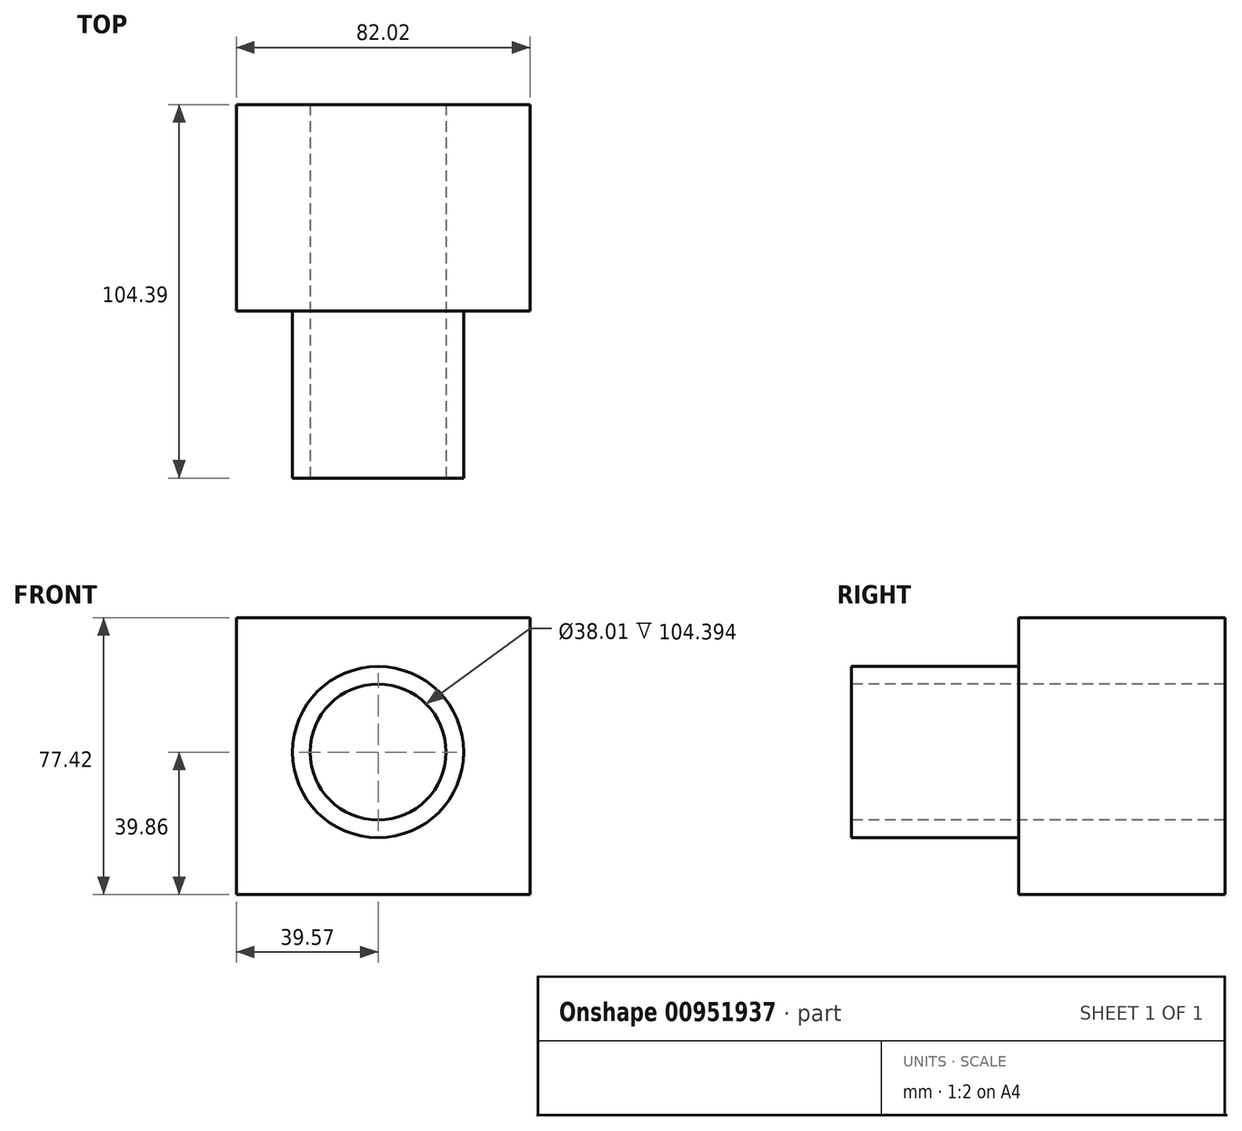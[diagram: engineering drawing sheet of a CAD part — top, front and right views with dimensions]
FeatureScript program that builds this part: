
annotation { "Feature Type Name" : "Feature", "Feature Type Description" : "" }
export const myFeature = defineFeature(function(context is Context, id is Id, definition is map)
    precondition{}
    {
        {
            var Q0;
            Q0=qCreatedBy(makeId("Front.planeOp"),FACE);
            var sketch = newSketch(context, id + "F0", { "sketchPlane" : qUnion([Q0])});
            skLineSegment(sketch, "E0.bottom", {"start": v(-39.57, 37.56) * mm, "end": v(42.45, 37.56) * mm});
            skLineSegment(sketch, "E0.top", {"start": v(-39.57, -39.86) * mm, "end": v(42.45, -39.86) * mm});
            skLineSegment(sketch, "E0.left", {"start": v(-39.57, 37.56) * mm, "end": v(-39.57, -39.86) * mm});
            skLineSegment(sketch, "E0.right", {"start": v(42.45, 37.56) * mm, "end": v(42.45, -39.86) * mm});
            skSolve(sketch);
        }
        {
            var Q0;
            Q0=makeQuery(id+"F0.imprint","IMPRINT",FACE,{"disambiguationData":[TD([[makeQuery(id+"F0.imprint","IMPRINT",EDGE,{"derivedFrom":sQuery(id+"F0.wireOp",EDGE,"E0.bottom")}),-1.0]])]});
            extrude(context, id + "F1", {"entities" : qUnion([Q0]), "depth" : 57.66 * mm, "offsetDistance" : 25.4 * mm});
        }
        {
            var Q0;
            Q0=makeQuery(id+"F1.opExtrude","CAP_FACE",FACE,{"disambiguationData":[OSD([sQuery(id+"F0.wireOp",EDGE,"E0.bottom"),sQuery(id+"F0.wireOp",EDGE,"E0.top"),sQuery(id+"F0.wireOp",EDGE,"E0.left"),sQuery(id+"F0.wireOp",EDGE,"E0.right")])],"isStart":false});
            var sketch = newSketch(context, id + "F2", { "sketchPlane" : qUnion([Q0])});
            skCircle(sketch, "E1", {"center": v(0, 0) * mm, "radius": 23.9 * mm});
            skSolve(sketch);
        }
        {
            var Q0;
            Q0=makeQuery(id+"F2.imprint","IMPRINT",FACE,{"disambiguationData":[TD([[makeQuery(id+"F2.imprint","IMPRINT",EDGE,{"derivedFrom":sQuery(id+"F2.wireOp",EDGE,"E1")}),1.0]])]});
            extrude(context, id + "F3", {"entities" : qUnion([Q0]), "operationType" : NewBodyOperationType.ADD, "depth" : 46.74 * mm, "offsetDistance" : 25.4 * mm});
        }
        {
            var Q0;
            Q0=makeQuery(id+"F3.opExtrude","CAP_FACE",FACE,{"disambiguationData":[OSD([sQuery(id+"F2.wireOp",EDGE,"E1")])],"isStart":false});
            var sketch = newSketch(context, id + "F4", { "sketchPlane" : qUnion([Q0])});
            skCircle(sketch, "E2", {"center": v(0, 0) * mm, "radius": 19 * mm});
            skSolve(sketch);
        }
        {
            var Q0;
            Q0=makeQuery(id+"F4.imprint","IMPRINT",FACE,{"disambiguationData":[TD([[makeQuery(id+"F4.imprint","IMPRINT",EDGE,{"derivedFrom":sQuery(id+"F4.wireOp",EDGE,"E2")}),1.0]])]});
            extrude(context, id + "F5", {"entities" : qUnion([Q0]), "operationType" : NewBodyOperationType.REMOVE, "oppositeDirection" : true, "depth" : 198.88 * mm, "offsetDistance" : 25.4 * mm});
        }
    });
